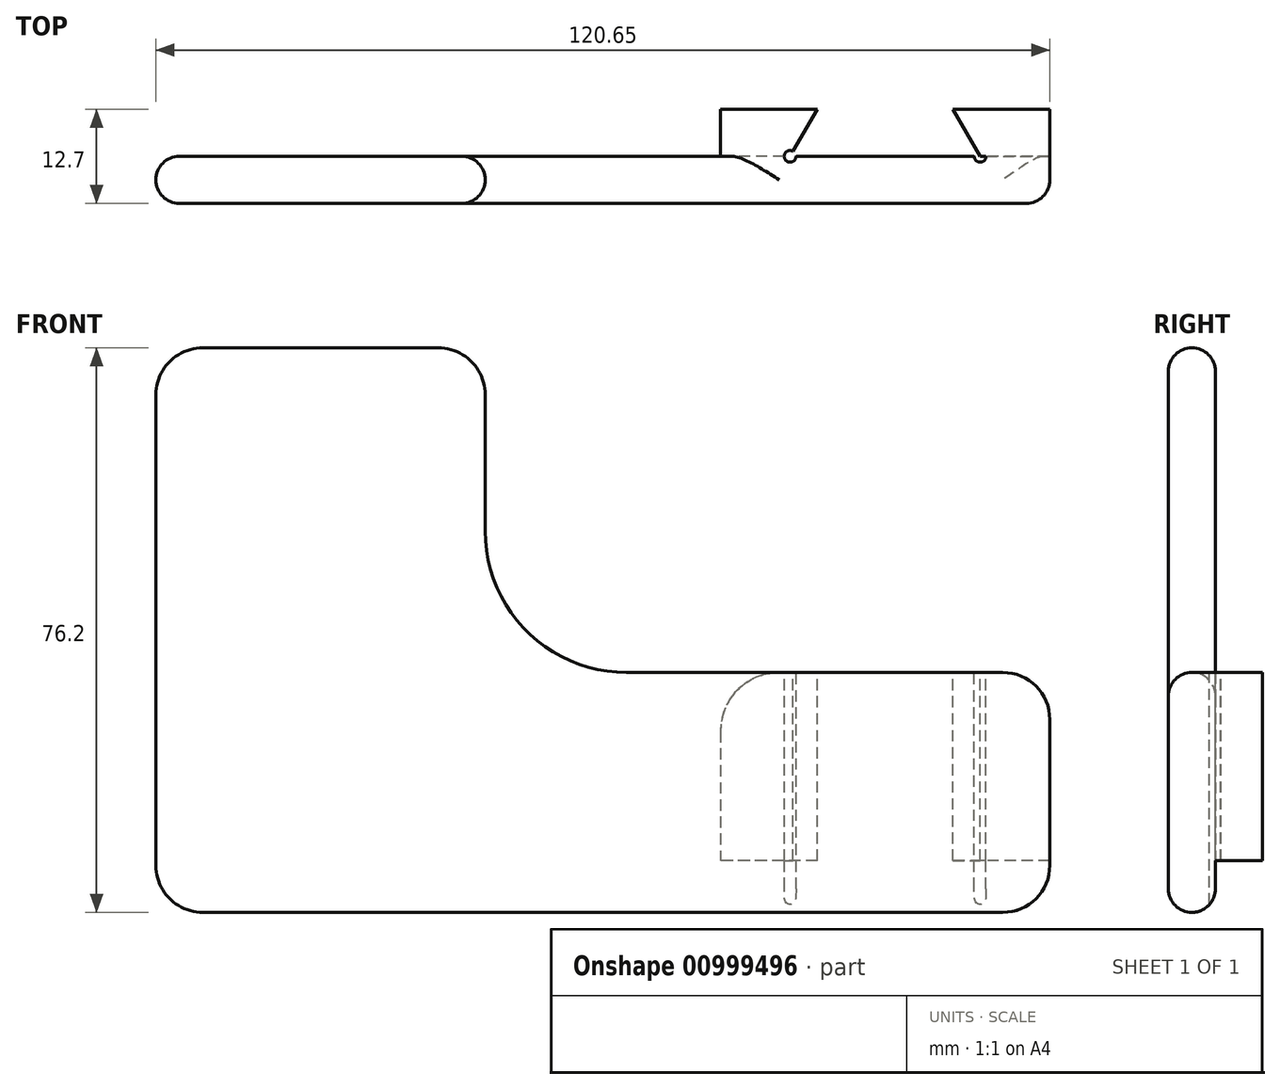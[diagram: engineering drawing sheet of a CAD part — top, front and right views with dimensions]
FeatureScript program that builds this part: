
annotation { "Feature Type Name" : "Feature", "Feature Type Description" : "" }
export const myFeature = defineFeature(function(context is Context, id is Id, definition is map)
    precondition{}
    {
        {
            var Q0;
            Q0=qCreatedBy(makeId("Front.planeOp"),FACE);
            var sketch = newSketch(context, id + "F0", { "sketchPlane" : qUnion([Q0])});
            skLineSegment(sketch, "E0", {"start": v(0, -21.7) * mm, "end": v(-120.65, -21.7) * mm});
            skLineSegment(sketch, "E1", {"start": v(-120.65, -21.7) * mm, "end": v(-120.65, 54.5) * mm});
            skLineSegment(sketch, "E2", {"start": v(-120.65, 54.5) * mm, "end": v(-76.2, 54.5) * mm});
            skLineSegment(sketch, "E3", {"start": v(-76.2, 54.5) * mm, "end": v(-76.2, 10.68) * mm});
            skLineSegment(sketch, "E4", {"start": v(-76.2, 10.68) * mm, "end": v(0, 10.68) * mm});
            skLineSegment(sketch, "E5", {"start": v(0, 10.68) * mm, "end": v(0, -21.7) * mm});
            skSolve(sketch);
        }
        {
            var Q0;
            Q0=makeQuery(id+"F0.imprint","IMPRINT",FACE,{"disambiguationData":[TD([[makeQuery(id+"F0.imprint","IMPRINT",EDGE,{"derivedFrom":sQuery(id+"F0.wireOp",EDGE,"E0")}),-1.0]])]});
            extrude(context, id + "F1", {"entities" : qUnion([Q0]), "depth" : 6.35 * mm, "offsetDistance" : 25.4 * mm});
        }
        {
            var Q0;
            Q0=makeQuery(id+"F1.opExtrude","CAP_FACE",FACE,{"disambiguationData":[OSD([sQuery(id+"F0.wireOp",EDGE,"E0"),sQuery(id+"F0.wireOp",EDGE,"E1"),sQuery(id+"F0.wireOp",EDGE,"E2"),sQuery(id+"F0.wireOp",EDGE,"E3"),sQuery(id+"F0.wireOp",EDGE,"E4"),sQuery(id+"F0.wireOp",EDGE,"E5")])],"isStart":true});
            var sketch = newSketch(context, id + "F2", { "sketchPlane" : qUnion([Q0])});
            skLineSegment(sketch, "E6.bottom", {"start": v(0, 10.68) * mm, "end": v(44.45, 10.68) * mm});
            skLineSegment(sketch, "E6.top", {"start": v(0, -21.7) * mm, "end": v(44.45, -21.7) * mm});
            skLineSegment(sketch, "E6.left", {"start": v(0, 10.68) * mm, "end": v(0, -21.7) * mm});
            skLineSegment(sketch, "E6.right", {"start": v(44.45, 10.68) * mm, "end": v(44.45, -21.7) * mm});
            skSolve(sketch);
        }
        {
            var Q0;
            Q0=makeQuery(id+"F2.imprint","IMPRINT",FACE,{"disambiguationData":[TD([[makeQuery(id+"F2.imprint","IMPRINT",EDGE,{"derivedFrom":sQuery(id+"F2.wireOp",EDGE,"E6.bottom")}),1.0]])]});
            extrude(context, id + "F3", {"entities" : qUnion([Q0]), "operationType" : NewBodyOperationType.ADD, "depth" : 6.35 * mm, "offsetDistance" : 25.4 * mm});
        }
        {
            var Q0;
            Q0=makeQuery(id+"F3.boolean.opBoolean","MERGE",FACE,{"derivedFrom":[makeQuery(id+"F1.opExtrude","SWEPT_FACE",FACE,{"disambiguationData":[OSD([sQuery(id+"F0.wireOp",EDGE,"E4")])]}),makeQuery(id+"F3.opExtrude","SWEPT_FACE",FACE,{"disambiguationData":[OSD([sQuery(id+"F2.wireOp",EDGE,"E6.bottom")])]})]});
            var sketch = newSketch(context, id + "F4", { "sketchPlane" : qUnion([Q0])});
            skLineSegment(sketch, "E7", {"start": v(-44.45, 0) * mm, "end": v(0, 0) * mm});
            skLineSegment(sketch, "E8", {"start": v(-22.23, 6.35) * mm, "end": v(-22.23, 0) * mm, "construction": true});
            skLineSegment(sketch, "E9", {"start": v(-13.06, 6.35) * mm, "end": v(-9.4, 0) * mm});
            skLineSegment(sketch, "E10.MirrorCS", {"start": v(-31.39, 6.35) * mm, "end": v(-35.05, 0) * mm});
            skCircle(sketch, "E11", {"center": v(-35.05, 0) * mm, "radius": 0.8 * mm});
            skCircle(sketch, "E12.MirrorC", {"center": v(-9.4, 0) * mm, "radius": 0.8 * mm});
            skSolve(sketch);
        }
        {
            var Q0;
            {var subQ2=sQuery(id+"F4.wireOp",EDGE,"E9");Q0=makeQuery(id+"F4.imprint","IMPRINT",FACE,{"disambiguationData":[TD([[makeQuery(id+"F4.imprint","IMPRINT",EDGE,{"derivedFrom":subQ2}),-1.0]])]});}
            var Q1;
            {var subQ0=sQuery(id+"F4.wireOp",EDGE,"E11");var subQ1=sQuery(id+"F4.wireOp",EDGE,"E7");var subQ2=makeQuery(id+"F4.imprint","INTERSECT",VERTEX,{"disambiguationData":[OD(0.0)],"derivedFrom":[subQ1,subQ0]});Q1=makeQuery(id+"F4.imprint","IMPRINT",FACE,{"disambiguationData":[TD([[makeQuery(id+"F4.imprint","IMPRINT",EDGE,{"disambiguationData":[TD([[subQ2,-1.0]])],"derivedFrom":subQ1}),1.0]])]});}
            var Q2;
            {var subQ0=sQuery(id+"F4.wireOp",EDGE,"E11");var subQ1=sQuery(id+"F4.wireOp",EDGE,"E7");var subQ2=makeQuery(id+"F4.imprint","INTERSECT",VERTEX,{"disambiguationData":[OD(0.0)],"derivedFrom":[subQ1,subQ0]});Q2=makeQuery(id+"F4.imprint","IMPRINT",FACE,{"disambiguationData":[TD([[makeQuery(id+"F4.imprint","IMPRINT",EDGE,{"disambiguationData":[TD([[subQ2,1.0]])],"derivedFrom":subQ1}),-1.0]])]});}
            var Q3;
            {var subQ0=sQuery(id+"F4.wireOp",EDGE,"E11");var subQ1=sQuery(id+"F4.wireOp",EDGE,"E7");var subQ2=makeQuery(id+"F4.imprint","INTERSECT",VERTEX,{"disambiguationData":[OD(0.0)],"derivedFrom":[subQ1,subQ0]});Q3=makeQuery(id+"F4.imprint","IMPRINT",FACE,{"disambiguationData":[TD([[makeQuery(id+"F4.imprint","IMPRINT",EDGE,{"disambiguationData":[TD([[subQ2,1.0]])],"derivedFrom":subQ1}),1.0]])]});}
            var Q4;
            {var subQ0=sQuery(id+"F4.wireOp",EDGE,"E10.MirrorCS");var subQ1=sQuery(id+"F4.wireOp",EDGE,"E7");var subQ2=makeQuery(id+"F4.imprint","INTERSECT",VERTEX,{"derivedFrom":[subQ1,subQ0]});Q4=makeQuery(id+"F4.imprint","IMPRINT",FACE,{"disambiguationData":[TD([[makeQuery(id+"F4.imprint","IMPRINT",EDGE,{"disambiguationData":[TD([[subQ2,1.0]])],"derivedFrom":subQ1}),1.0]])]});}
            var Q5;
            {var subQ0=sQuery(id+"F4.wireOp",EDGE,"E12.MirrorC");var subQ1=sQuery(id+"F4.wireOp",EDGE,"E7");var subQ2=makeQuery(id+"F4.imprint","INTERSECT",VERTEX,{"disambiguationData":[OD(0.0)],"derivedFrom":[subQ1,subQ0]});Q5=makeQuery(id+"F4.imprint","IMPRINT",FACE,{"disambiguationData":[TD([[makeQuery(id+"F4.imprint","IMPRINT",EDGE,{"disambiguationData":[TD([[subQ2,1.0]])],"derivedFrom":subQ1}),1.0]])]});}
            var Q6;
            {var subQ0=sQuery(id+"F4.wireOp",EDGE,"E7");var subQ1=makeQuery(id+"F4.imprint","INTERSECT",VERTEX,{"derivedFrom":[subQ0,sQuery(id+"F4.wireOp",EDGE,"E9")]});Q6=makeQuery(id+"F4.imprint","IMPRINT",FACE,{"disambiguationData":[TD([[makeQuery(id+"F4.imprint","IMPRINT",EDGE,{"disambiguationData":[TD([[subQ1,1.0]])],"derivedFrom":subQ0}),-1.0]])]});}
            extrude(context, id + "F5", {"entities" : qUnion([Q0, Q1, Q2, Q3, Q4, Q5, Q6]), "operationType" : NewBodyOperationType.REMOVE, "endBound" : BoundingType.THROUGH_ALL, "oppositeDirection" : true, "depth" : 25.4 * mm, "offsetDistance" : 25.4 * mm});
        }
        {
            var Q0;
            {var subQ0=sQuery(id+"F2.wireOp",EDGE,"E6.bottom");var subQ1=sQuery(id+"F2.wireOp",EDGE,"E6.top");var subQ2=sQuery(id+"F2.wireOp",EDGE,"E6.left");Q0=makeQuery(id+"F5.boolean.opBoolean","SPLIT",FACE,{"disambiguationData":[TD([makeQuery(id+"F1.opExtrude","SWEPT_FACE",FACE,{"disambiguationData":[OSD([sQuery(id+"F0.wireOp",EDGE,"E5")])]})])],"derivedFrom":makeQuery(id+"F3.opExtrude","CAP_FACE",FACE,{"disambiguationData":[OSD([subQ0,subQ1,subQ2,sQuery(id+"F2.wireOp",EDGE,"E6.right")])],"isStart":false})});}
            var sketch = newSketch(context, id + "F6", { "sketchPlane" : qUnion([Q0])});
            skLineSegment(sketch, "E13.bottom", {"start": v(0, -21.7) * mm, "end": v(44.45, -21.7) * mm});
            skLineSegment(sketch, "E13.top", {"start": v(0, -14.72) * mm, "end": v(44.45, -14.72) * mm});
            skLineSegment(sketch, "E13.left", {"start": v(0, -21.7) * mm, "end": v(0, -14.72) * mm});
            skLineSegment(sketch, "E13.right", {"start": v(44.45, -21.7) * mm, "end": v(44.45, -14.72) * mm});
            skSolve(sketch);
        }
        {
            var Q0;
            {var subQ0=sQuery(id+"F6.wireOp",EDGE,"E13.left");Q0=makeQuery(id+"F6.imprint","IMPRINT",FACE,{"disambiguationData":[TD([[makeQuery(id+"F6.imprint","IMPRINT",EDGE,{"derivedFrom":subQ0}),1.0]])]});}
            var Q1;
            {var subQ3=sQuery(id+"F6.wireOp",EDGE,"E13.right");Q1=makeQuery(id+"F6.imprint","IMPRINT",FACE,{"disambiguationData":[TD([[makeQuery(id+"F6.imprint","IMPRINT",EDGE,{"derivedFrom":subQ3}),1.0]])]});}
            var Q2;
            Q2=makeQuery(id+"F5.boolean.opBoolean","COPY",FACE,{"derivedFrom":makeQuery(id+"F5.opExtrude","SWEPT_FACE",FACE,{"disambiguationData":[OSD([sQuery(id+"F4.wireOp",EDGE,"E7")])]})});
            extrude(context, id + "F7", {"entities" : qUnion([Q0, Q1]), "operationType" : NewBodyOperationType.REMOVE, "endBound" : BoundingType.UP_TO_SURFACE, "oppositeDirection" : true, "depth" : 25.4 * mm, "endBoundEntityFace" : qUnion([Q2]), "offsetDistance" : 25.4 * mm});
        }
        {
            var Q0;
            Q0=makeQuery(id+"F1.opExtrude","SWEPT_EDGE",EDGE,{"disambiguationData":[OSD([sQuery(id+"F0.wireOp",EDGE,"E2"),sQuery(id+"F0.wireOp",EDGE,"E3")])]});
            var Q1;
            Q1=makeQuery(id+"F1.opExtrude","SWEPT_EDGE",EDGE,{"disambiguationData":[OSD([sQuery(id+"F0.wireOp",EDGE,"E1"),sQuery(id+"F0.wireOp",EDGE,"E2")])]});
            var Q2;
            Q2=makeQuery(id+"F1.opExtrude","SWEPT_EDGE",EDGE,{"disambiguationData":[OSD([sQuery(id+"F0.wireOp",EDGE,"E0"),sQuery(id+"F0.wireOp",EDGE,"E1")])]});
            var Q3;
            Q3=makeQuery(id+"F3.boolean.opBoolean","MERGE",EDGE,{"derivedFrom":[makeQuery(id+"F1.opExtrude","SWEPT_EDGE",EDGE,{"disambiguationData":[OSD([sQuery(id+"F0.wireOp",EDGE,"E4"),sQuery(id+"F0.wireOp",EDGE,"E5")])]}),makeQuery(id+"F3.opExtrude","SWEPT_EDGE",EDGE,{"disambiguationData":[OSD([sQuery(id+"F2.wireOp",EDGE,"E6.bottom"),sQuery(id+"F2.wireOp",EDGE,"E6.left")])]})]});
            var Q4;
            Q4=makeQuery(id+"F3.boolean.opBoolean","MERGE",EDGE,{"derivedFrom":[makeQuery(id+"F1.opExtrude","SWEPT_EDGE",EDGE,{"disambiguationData":[OSD([sQuery(id+"F0.wireOp",EDGE,"E0"),sQuery(id+"F0.wireOp",EDGE,"E5")])]}),makeQuery(id+"F3.opExtrude","SWEPT_EDGE",EDGE,{"disambiguationData":[OSD([sQuery(id+"F2.wireOp",EDGE,"E6.top"),sQuery(id+"F2.wireOp",EDGE,"E6.left")])]})]});
            fillet(context, id + "F8", {"entities" : qUnion([Q0, Q1, Q2, Q3, Q4]), "tangentPropagation" : true, "radius" : 6.35 * mm, "defaultsChanged" : false, "vertexSettings" : [], "allowEdgeOverflow" : false});
        }
        {
            var Q0;
            Q0=makeQuery(id+"F1.opExtrude","SWEPT_EDGE",EDGE,{"disambiguationData":[OSD([sQuery(id+"F0.wireOp",EDGE,"E3"),sQuery(id+"F0.wireOp",EDGE,"E4")])]});
            fillet(context, id + "F9", {"entities" : qUnion([Q0]), "tangentPropagation" : true, "radius" : 19.05 * mm, "defaultsChanged" : false, "vertexSettings" : [], "allowEdgeOverflow" : false});
        }
        {
            var Q0;
            Q0=makeQuery(id+"F1.opExtrude","CAP_FACE",FACE,{"disambiguationData":[OSD([sQuery(id+"F0.wireOp",EDGE,"E0"),sQuery(id+"F0.wireOp",EDGE,"E1"),sQuery(id+"F0.wireOp",EDGE,"E2"),sQuery(id+"F0.wireOp",EDGE,"E3"),sQuery(id+"F0.wireOp",EDGE,"E4"),sQuery(id+"F0.wireOp",EDGE,"E5")])],"isStart":false});
            var Q1;
            Q1=makeQuery(id+"F1.opExtrude","CAP_EDGE",EDGE,{"disambiguationData":[OSD([sQuery(id+"F0.wireOp",EDGE,"E2")])],"isStart":true});
            fillet(context, id + "F10", {"entities" : qUnion([Q0, Q1]), "tangentPropagation" : true, "radius" : 3.17 * mm, "defaultsChanged" : false, "vertexSettings" : [], "allowEdgeOverflow" : false});
        }
        {
            var Q0;
            Q0=makeQuery(id+"F3.opExtrude","SWEPT_EDGE",EDGE,{"disambiguationData":[OSD([sQuery(id+"F0.wireOp",EDGE,"E4"),sQuery(id+"F2.wireOp",EDGE,"E6.bottom"),sQuery(id+"F2.wireOp",EDGE,"E6.right")])]});
            fillet(context, id + "F11", {"entities" : qUnion([Q0]), "tangentPropagation" : true, "radius" : 7.94 * mm, "defaultsChanged" : true, "vertexSettings" : [], "allowEdgeOverflow" : false});
        }
    });
